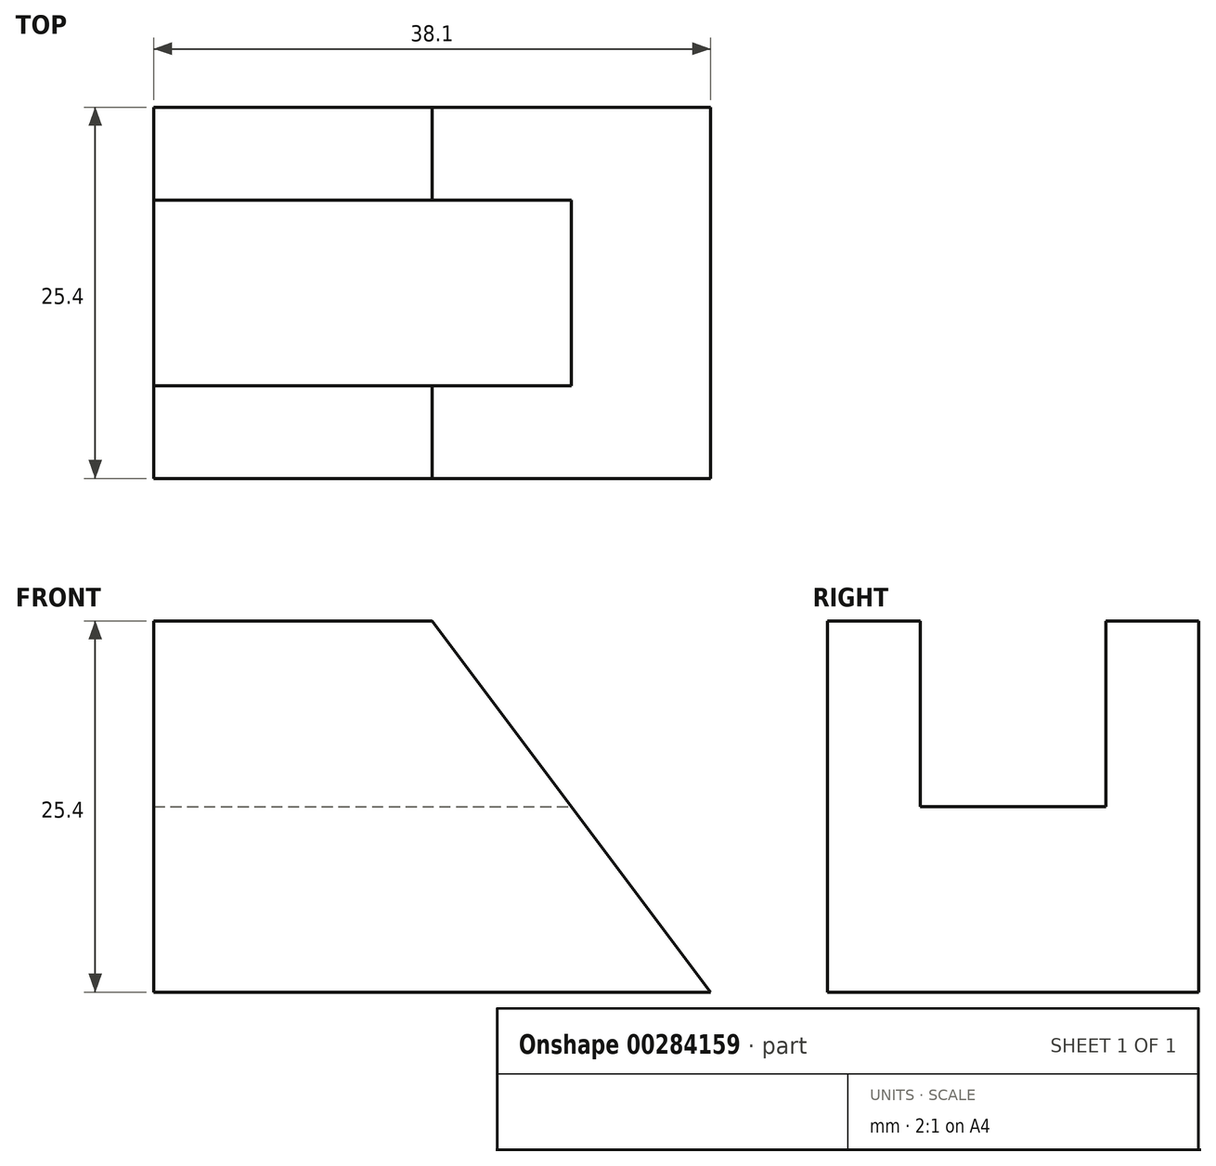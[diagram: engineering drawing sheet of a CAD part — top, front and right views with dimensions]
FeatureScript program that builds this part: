
annotation { "Feature Type Name" : "Feature", "Feature Type Description" : "" }
export const myFeature = defineFeature(function(context is Context, id is Id, definition is map)
    precondition{}
    {
        {
            var Q0;
            Q0=qCreatedBy(makeId("Front.planeOp"),FACE);
            var sketch = newSketch(context, id + "F0", { "sketchPlane" : qUnion([Q0])});
            skLineSegment(sketch, "E0", {"start": v(0, 0) * mm, "end": v(0, 25.4) * mm});
            skLineSegment(sketch, "E1", {"start": v(0, 25.4) * mm, "end": v(19.05, 25.4) * mm});
            skLineSegment(sketch, "E2", {"start": v(19.05, 25.4) * mm, "end": v(38.1, 0) * mm});
            skLineSegment(sketch, "E3", {"start": v(38.1, 0) * mm, "end": v(0, 0) * mm});
            skSolve(sketch);
        }
        {
            var Q0;
            Q0=makeQuery(id+"F0.imprint","IMPRINT",FACE,{"disambiguationData":[TD([[makeQuery(id+"F0.imprint","IMPRINT",EDGE,{"derivedFrom":sQuery(id+"F0.wireOp",EDGE,"E0")}),-1.0]])]});
            extrude(context, id + "F1", {"entities" : qUnion([Q0]), "oppositeDirection" : true, "depth" : 25.4 * mm});
        }
        {
            var Q0;
            Q0=makeQuery(id+"F1.opExtrude","SWEPT_FACE",FACE,{"disambiguationData":[OSD([sQuery(id+"F0.wireOp",EDGE,"E1")])]});
            var sketch = newSketch(context, id + "F2", { "sketchPlane" : qUnion([Q0])});
            skLineSegment(sketch, "E4", {"start": v(0, 19.05) * mm, "end": v(28.58, 19.05) * mm});
            skLineSegment(sketch, "E5", {"start": v(28.58, 19.05) * mm, "end": v(28.58, 6.35) * mm});
            skLineSegment(sketch, "E6", {"start": v(28.58, 6.35) * mm, "end": v(0, 6.35) * mm});
            skSolve(sketch);
        }
        {
            var Q0;
            {var subQ0=sQuery(id+"F2.wireOp",EDGE,"E4");var subQ1=sQuery(id+"F0.wireOp",EDGE,"E1");var subQ2=makeQuery(id+"F1.opExtrude","SWEPT_EDGE",EDGE,{"disambiguationData":[OSD([sQuery(id+"F0.wireOp",EDGE,"E0"),subQ1])]});var subQ3=makeQuery(id+"F2.imprint","INTERSECT",VERTEX,{"derivedFrom":[subQ2,subQ0]});Q0=makeQuery(id+"F2.imprint","IMPRINT",FACE,{"disambiguationData":[TD([[makeQuery(id+"F2.imprint","IMPRINT",EDGE,{"disambiguationData":[TD([[subQ3,-1.0]])],"derivedFrom":subQ0}),-1.0]])]});}
            var Q1;
            {var subQ0=sQuery(id+"F2.wireOp",EDGE,"E5");Q1=makeQuery(id+"F2.imprint","IMPRINT",FACE,{"disambiguationData":[TD([[makeQuery(id+"F2.imprint","IMPRINT",EDGE,{"derivedFrom":subQ0}),-1.0]])]});}
            extrude(context, id + "F3", {"entities" : qUnion([Q0, Q1]), "operationType" : NewBodyOperationType.REMOVE, "oppositeDirection" : true, "depth" : 12.7 * mm});
        }
    });
